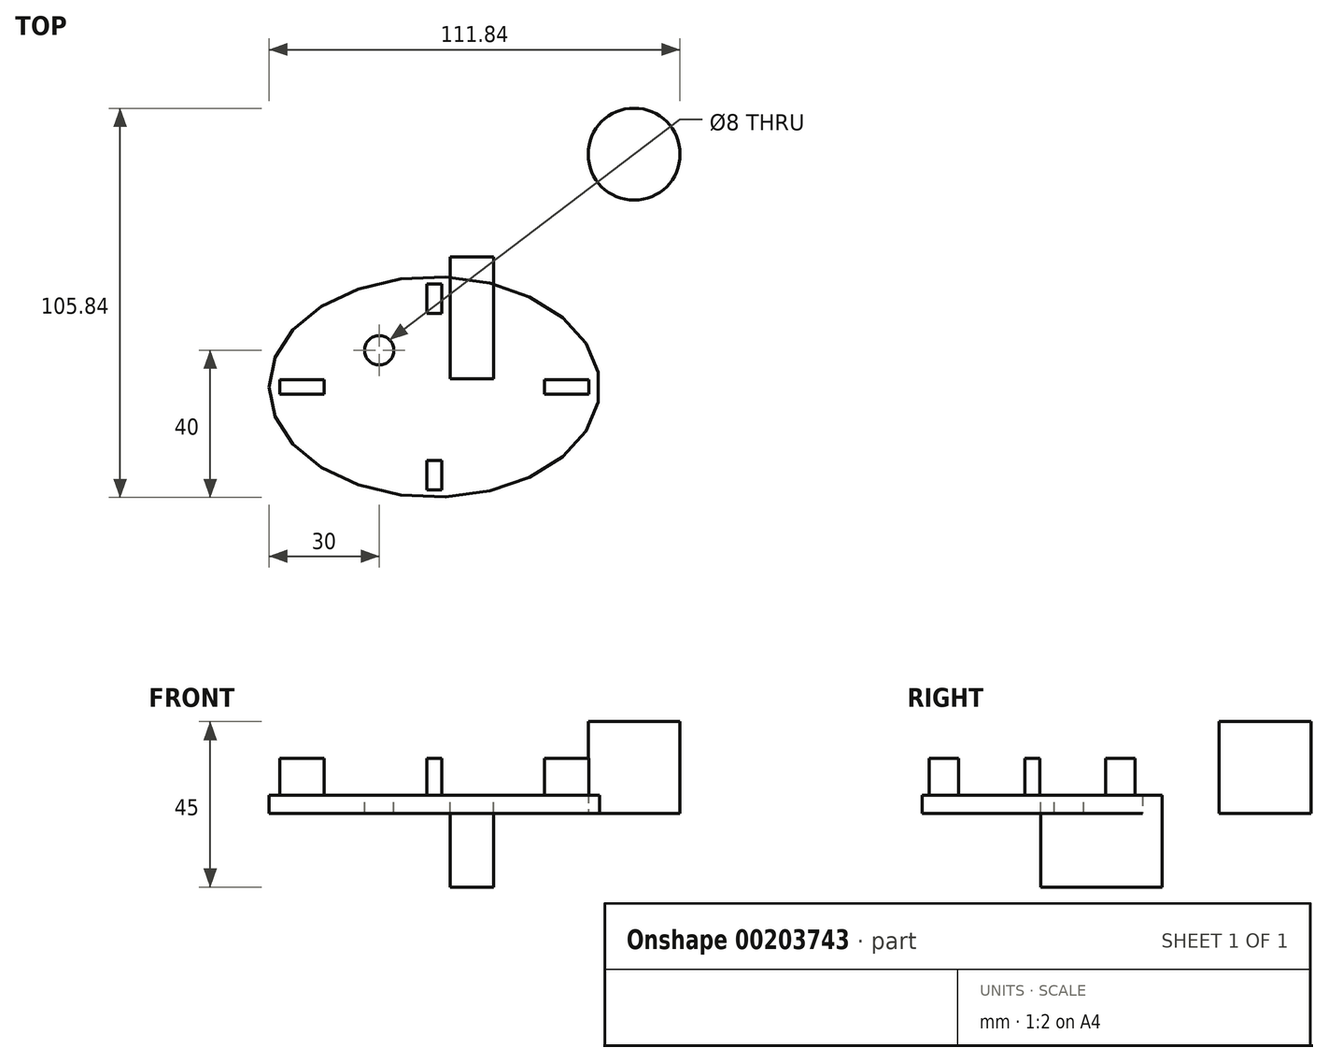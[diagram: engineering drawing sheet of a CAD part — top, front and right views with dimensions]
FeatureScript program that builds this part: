
annotation { "Feature Type Name" : "Feature", "Feature Type Description" : "" }
export const myFeature = defineFeature(function(context is Context, id is Id, definition is map)
    precondition{}
    {
        {
            var Q0;
            Q0=qCreatedBy(makeId("Top.planeOp"),FACE);
            var sketch = newSketch(context, id + "F0", { "sketchPlane" : qUnion([Q0])});
            skEllipse(sketch, "E0", {"center": v(0, 0) * mm, "majorRadius": 45 * mm, "minorRadius": 30 * mm, "majorAxis": v(-1, 0)});
            skSolve(sketch);
        }
        {
            var Q0;
            Q0=makeQuery(id+"F0.imprint","IMPRINT",FACE,{"disambiguationData":[TD([[makeQuery(id+"F0.imprint","IMPRINT",EDGE,{"derivedFrom":sQuery(id+"F0.wireOp",EDGE,"E0")}),1.0]])]});
            extrude(context, id + "F1", {"entities" : qUnion([Q0]), "depth" : 5 * mm});
        }
        {
            var Q0;
            Q0=makeQuery(id+"F1.opExtrude","CAP_FACE",FACE,{"disambiguationData":[OSD([sQuery(id+"F0.wireOp",EDGE,"E0")])],"isStart":false});
            var sketch = newSketch(context, id + "F2", { "sketchPlane" : qUnion([Q0])});
            skLineSegment(sketch, "E1.bottom", {"start": v(-42, 2) * mm, "end": v(-30, 2) * mm});
            skLineSegment(sketch, "E1.top", {"start": v(-42, -2) * mm, "end": v(-30, -2) * mm});
            skLineSegment(sketch, "E1.left", {"start": v(-42, 2) * mm, "end": v(-42, -2) * mm});
            skLineSegment(sketch, "E1.right", {"start": v(-30, 2) * mm, "end": v(-30, -2) * mm});
            skLineSegment(sketch, "E2.bottom", {"start": v(30, 2) * mm, "end": v(42, 2) * mm});
            skLineSegment(sketch, "E2.top", {"start": v(30, -2) * mm, "end": v(42, -2) * mm});
            skLineSegment(sketch, "E2.left", {"start": v(30, 2) * mm, "end": v(30, -2) * mm});
            skLineSegment(sketch, "E2.right", {"start": v(42, 2) * mm, "end": v(42, -2) * mm});
            skLineSegment(sketch, "E3.bottom", {"start": v(-2, 28) * mm, "end": v(2, 28) * mm});
            skLineSegment(sketch, "E3.top", {"start": v(-2, 20) * mm, "end": v(2, 20) * mm});
            skLineSegment(sketch, "E3.left", {"start": v(-2, 28) * mm, "end": v(-2, 20) * mm});
            skLineSegment(sketch, "E3.right", {"start": v(2, 28) * mm, "end": v(2, 20) * mm});
            skLineSegment(sketch, "E4.bottom", {"start": v(-2, -20) * mm, "end": v(2, -20) * mm});
            skLineSegment(sketch, "E4.top", {"start": v(-2, -28) * mm, "end": v(2, -28) * mm});
            skLineSegment(sketch, "E4.left", {"start": v(-2, -20) * mm, "end": v(-2, -28) * mm});
            skLineSegment(sketch, "E4.right", {"start": v(2, -20) * mm, "end": v(2, -28) * mm});
            skSolve(sketch);
        }
        {
            var Q0;
            Q0=makeQuery(id+"F2.imprint","IMPRINT",FACE,{"disambiguationData":[TD([[makeQuery(id+"F2.imprint","IMPRINT",EDGE,{"derivedFrom":sQuery(id+"F2.wireOp",EDGE,"E1.bottom")}),-1.0]])]});
            var Q1;
            Q1=makeQuery(id+"F2.imprint","IMPRINT",FACE,{"disambiguationData":[TD([[makeQuery(id+"F2.imprint","IMPRINT",EDGE,{"derivedFrom":sQuery(id+"F2.wireOp",EDGE,"E3.bottom")}),-1.0]])]});
            var Q2;
            Q2=makeQuery(id+"F2.imprint","IMPRINT",FACE,{"disambiguationData":[TD([[makeQuery(id+"F2.imprint","IMPRINT",EDGE,{"derivedFrom":sQuery(id+"F2.wireOp",EDGE,"E2.bottom")}),-1.0]])]});
            var Q3;
            Q3=makeQuery(id+"F2.imprint","IMPRINT",FACE,{"disambiguationData":[TD([[makeQuery(id+"F2.imprint","IMPRINT",EDGE,{"derivedFrom":sQuery(id+"F2.wireOp",EDGE,"E4.bottom")}),-1.0]])]});
            extrude(context, id + "F3", {"entities" : qUnion([Q0, Q1, Q2, Q3]), "operationType" : NewBodyOperationType.ADD, "depth" : 10 * mm});
        }
        {
            var Q0;
            Q0=makeQuery(id+"F1.opExtrude","CAP_FACE",FACE,{"disambiguationData":[OSD([sQuery(id+"F0.wireOp",EDGE,"E0")])],"isStart":false});
            var sketch = newSketch(context, id + "F4", { "sketchPlane" : qUnion([Q0])});
            skCircle(sketch, "E5", {"center": v(-15, 10) * mm, "radius": 4 * mm});
            skSolve(sketch);
        }
        {
            var Q0;
            Q0=makeQuery(id+"F4.imprint","IMPRINT",FACE,{"disambiguationData":[TD([[makeQuery(id+"F4.imprint","IMPRINT",EDGE,{"derivedFrom":sQuery(id+"F4.wireOp",EDGE,"E5")}),1.0]])]});
            extrude(context, id + "F5", {"entities" : qUnion([Q0]), "operationType" : NewBodyOperationType.REMOVE, "oppositeDirection" : true, "depth" : 25 * mm});
        }
        {
            var Q0;
            Q0=makeQuery(id+"F1.opExtrude","CAP_FACE",FACE,{"disambiguationData":[OSD([sQuery(id+"F0.wireOp",EDGE,"E0")])],"isStart":false});
            var sketch = newSketch(context, id + "F6", { "sketchPlane" : qUnion([Q0])});
            skCircle(sketch, "E6", {"center": v(9.69, 29.3) * mm, "radius": 17.69 * mm});
            skSolve(sketch);
        }
        {
            var Q0;
            {var subQ0=sQuery(id+"F6.wireOp",EDGE,"E6");var subQ1=makeQuery(id+"F1.opExtrude","CAP_EDGE",EDGE,{"disambiguationData":[OSD([sQuery(id+"F0.wireOp",EDGE,"E0")])],"isStart":false});var subQ2=makeQuery(id+"F6.imprint","INTERSECT",VERTEX,{"disambiguationData":[OD(0.0)],"derivedFrom":[subQ1,subQ0]});Q0=makeQuery(id+"F6.imprint","IMPRINT",FACE,{"disambiguationData":[TD([[makeQuery(id+"F6.imprint","IMPRINT",EDGE,{"disambiguationData":[TD([[subQ2,1.0]])],"derivedFrom":subQ0}),1.0]])]});}
            extrude(context, id + "F11", {"entities" : qUnion([Q0]), "depth" : 25 * mm});
        }
        {
            var Q0;
            Q0=makeQuery(id+"F11.opExtrude","SWEPT_BODY",BODY,{"disambiguationData":[OSD([sQuery(id+"F0.wireOp",EDGE,"E0"),sQuery(id+"F6.wireOp",EDGE,"E6")])]});
            deleteBodies(context, id + "F7", {"entities" : qUnion([Q0])});
        }
        {
            var Q0;
            Q0=qCreatedBy(makeId("Top.planeOp"),FACE);
            var sketch = newSketch(context, id + "F8", { "sketchPlane" : qUnion([Q0])});
            skCircle(sketch, "E7", {"center": v(54.34, 63.34) * mm, "radius": 12.5 * mm});
            skCircle(sketch, "E8", {"center": v(47.54, 73.82) * mm, "radius": 12.5 * mm, "construction": true});
            skSolve(sketch);
        }
        {
            var Q0;
            Q0=makeQuery(id+"F8.imprint","IMPRINT",FACE,{"disambiguationData":[TD([[makeQuery(id+"F8.imprint","IMPRINT",EDGE,{"derivedFrom":sQuery(id+"F8.wireOp",EDGE,"E7")}),1.0]])]});
            extrude(context, id + "F9", {"entities" : qUnion([Q0]), "depth" : 25 * mm});
        }
        {
            var Q0;
            Q0=makeQuery(id+"F1.opExtrude","CAP_FACE",FACE,{"disambiguationData":[OSD([sQuery(id+"F0.wireOp",EDGE,"E0")])],"isStart":false});
            var sketch = newSketch(context, id + "F12", { "sketchPlane" : qUnion([Q0])});
            skLineSegment(sketch, "E9.bottom", {"start": v(16.06, 35.34) * mm, "end": v(4.32, 35.34) * mm});
            skLineSegment(sketch, "E9.top", {"start": v(16.06, 2.3) * mm, "end": v(4.32, 2.3) * mm});
            skLineSegment(sketch, "E9.left", {"start": v(16.06, 35.34) * mm, "end": v(16.06, 2.3) * mm});
            skLineSegment(sketch, "E9.right", {"start": v(4.32, 35.34) * mm, "end": v(4.32, 2.3) * mm});
            skPoint(sketch, "E9.middle", {"position": v(10.19, 18.82) * mm});
            skSolve(sketch);
        }
        {
            var Q0;
            Q0 = qSketchRegion(id + "F12", true);
            var Q1;
            {var subQ0=sQuery(id+"F12.wireOp",EDGE,"E9.bottom");Q1=makeQuery(id+"F12.imprint","IMPRINT",FACE,{"disambiguationData":[TD([[makeQuery(id+"F12.imprint","IMPRINT",EDGE,{"derivedFrom":subQ0}),1.0]])]});}
            extrude(context, id + "F10", {"entities" : qUnion([Q0, Q1]), "oppositeDirection" : true, "depth" : 25 * mm});
        }
    });
